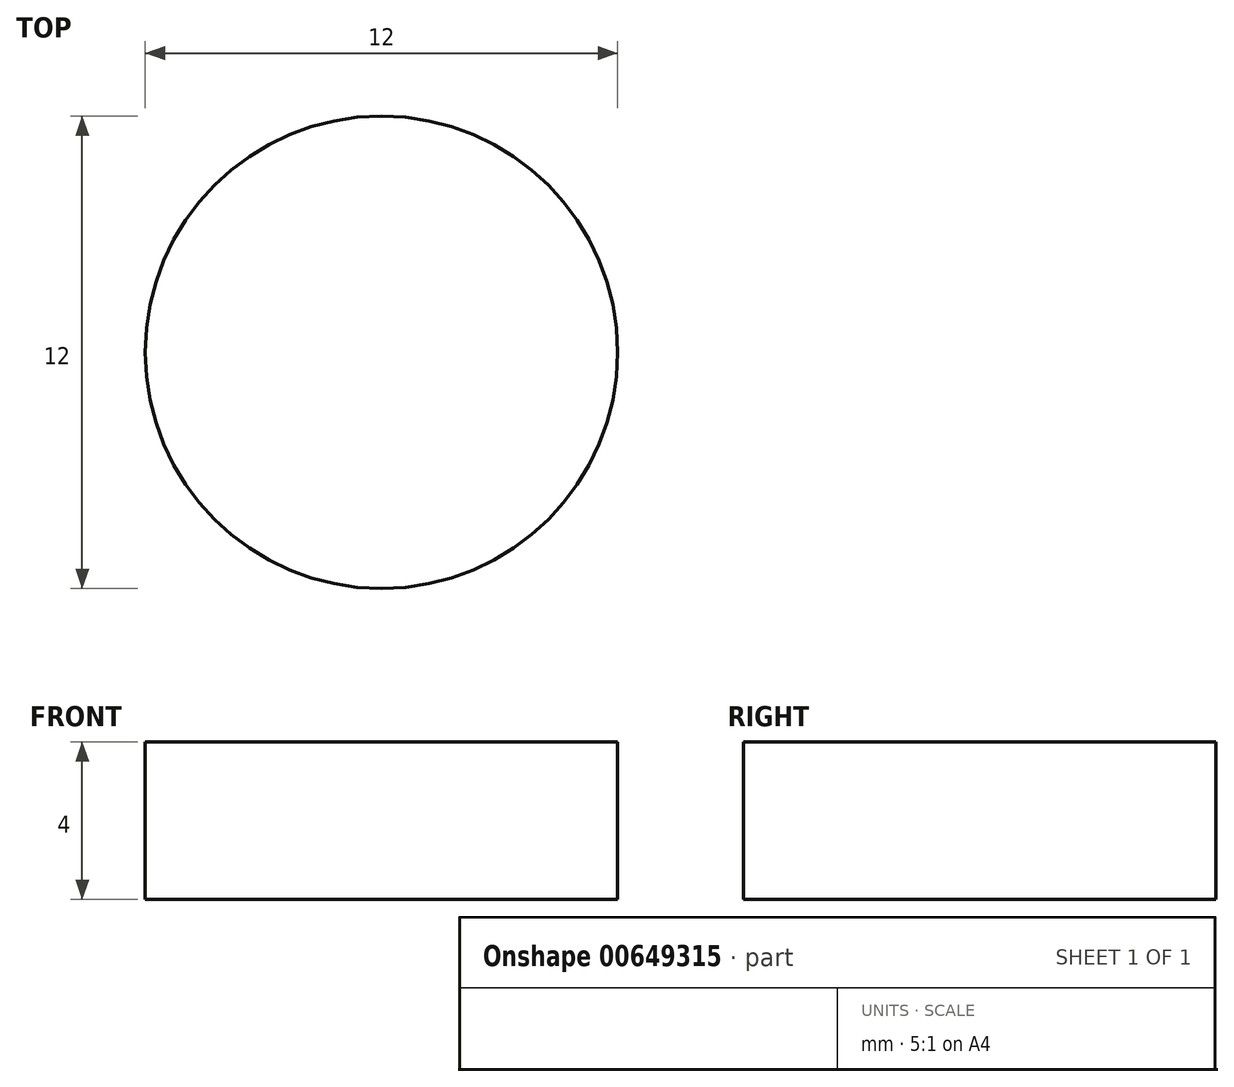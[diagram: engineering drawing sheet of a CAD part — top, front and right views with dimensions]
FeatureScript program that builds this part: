
annotation { "Feature Type Name" : "Feature", "Feature Type Description" : "" }
export const myFeature = defineFeature(function(context is Context, id is Id, definition is map)
    precondition{}
    {
        {
            var Q0;
            Q0=qCreatedBy(makeId("Top.planeOp"),FACE);
            var sketch = newSketch(context, id + "F0", { "sketchPlane" : qUnion([Q0])});
            skCircle(sketch, "E0", {"center": v(0, 0) * mm, "radius": 6 * mm});
            skSolve(sketch);
        }
        {
            var Q0;
            Q0=makeQuery(id+"F0.imprint","IMPRINT",FACE,{"disambiguationData":[TD([[makeQuery(id+"F0.imprint","IMPRINT",EDGE,{"derivedFrom":sQuery(id+"F0.wireOp",EDGE,"E0")}),1.0]])]});
            extrude(context, id + "F1", {"entities" : qUnion([Q0]), "depth" : 4 * mm, "offsetDistance" : 25 * mm});
        }
    });
